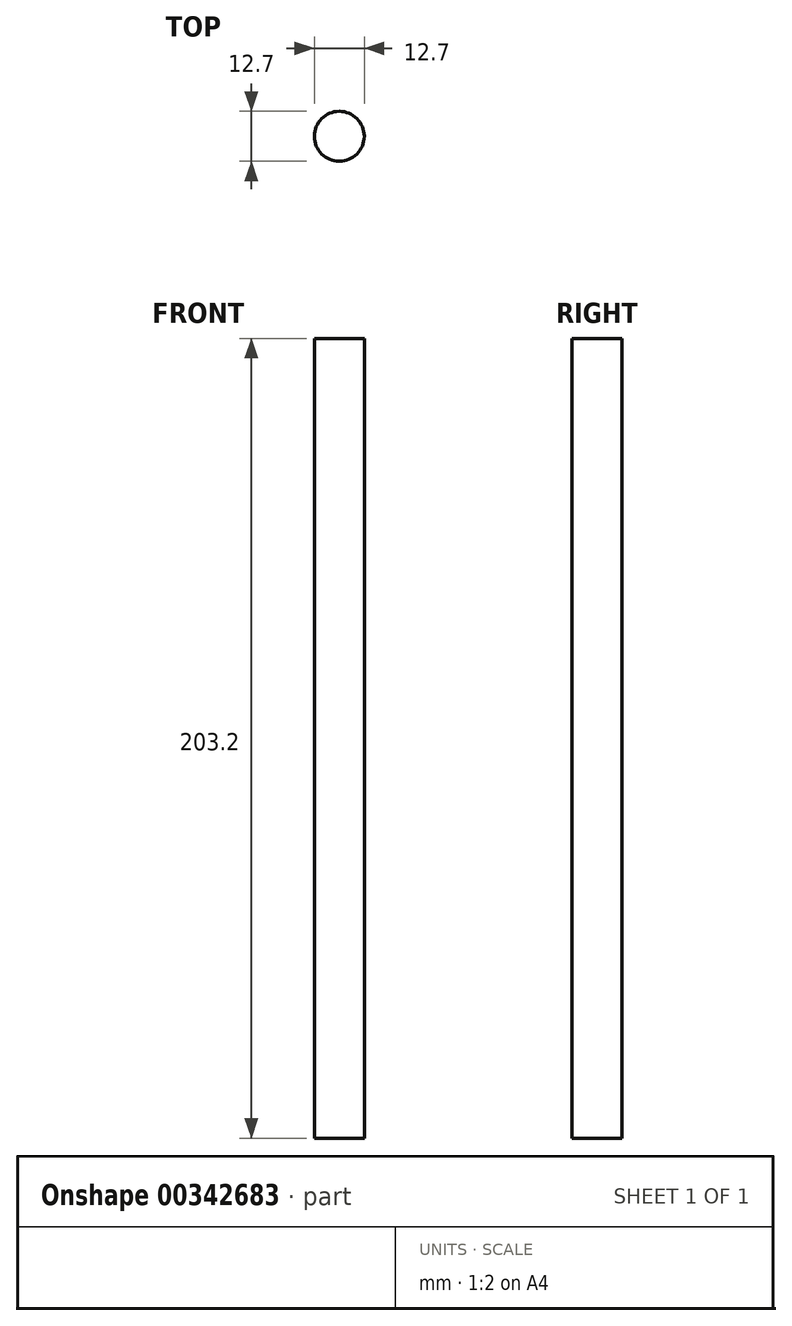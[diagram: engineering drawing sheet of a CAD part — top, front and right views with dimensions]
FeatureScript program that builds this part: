
annotation { "Feature Type Name" : "Feature", "Feature Type Description" : "" }
export const myFeature = defineFeature(function(context is Context, id is Id, definition is map)
    precondition{}
    {
        {
            var Q0;
            Q0=qCreatedBy(makeId("Top.planeOp"),FACE);
            var sketch = newSketch(context, id + "F0", { "sketchPlane" : qUnion([Q0])});
            skCircle(sketch, "E0", {"center": v(0, 0) * mm, "radius": 6.35 * mm});
            skSolve(sketch);
        }
        {
            var Q0;
            Q0 = qSketchRegion(id + "F0", true);
            extrude(context, id + "F1", {"entities" : qUnion([Q0]), "oppositeDirection" : true, "depth" : 203.2 * mm});
        }
    });
